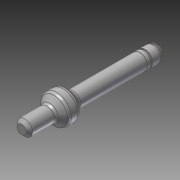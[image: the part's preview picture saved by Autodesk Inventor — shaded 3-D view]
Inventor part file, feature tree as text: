
AUTODESK INVENTOR PART (.ipt)
format: ipt  version: 2014 SP1 (Build 180222100, 222)  size: 116,224 bytes
history: native  units: in
note: dims shown in document units (in); Inventor stores cm internally (conversion verified against a paired STEP export)
features: chamfer x1, other x1, imported_body x1
ambient origin geometry x8: Origin, YZ Plane, XZ Plane, XY Plane, X Axis, Y Axis, Z Axis, Center Point
bodies: Body1 (feature_tree)
feature tree (3):
  chamfer  "Chamfer1"  [1 undecoded]
  other  "217-2790-004 Rev2.ipt1"
  imported_body  "Base1"
note: 1 required parameter value undecoded (feature->parameter linkage not recoverable at this tier; creation-order binding heuristic only, values carry confidence <= 0.55)
